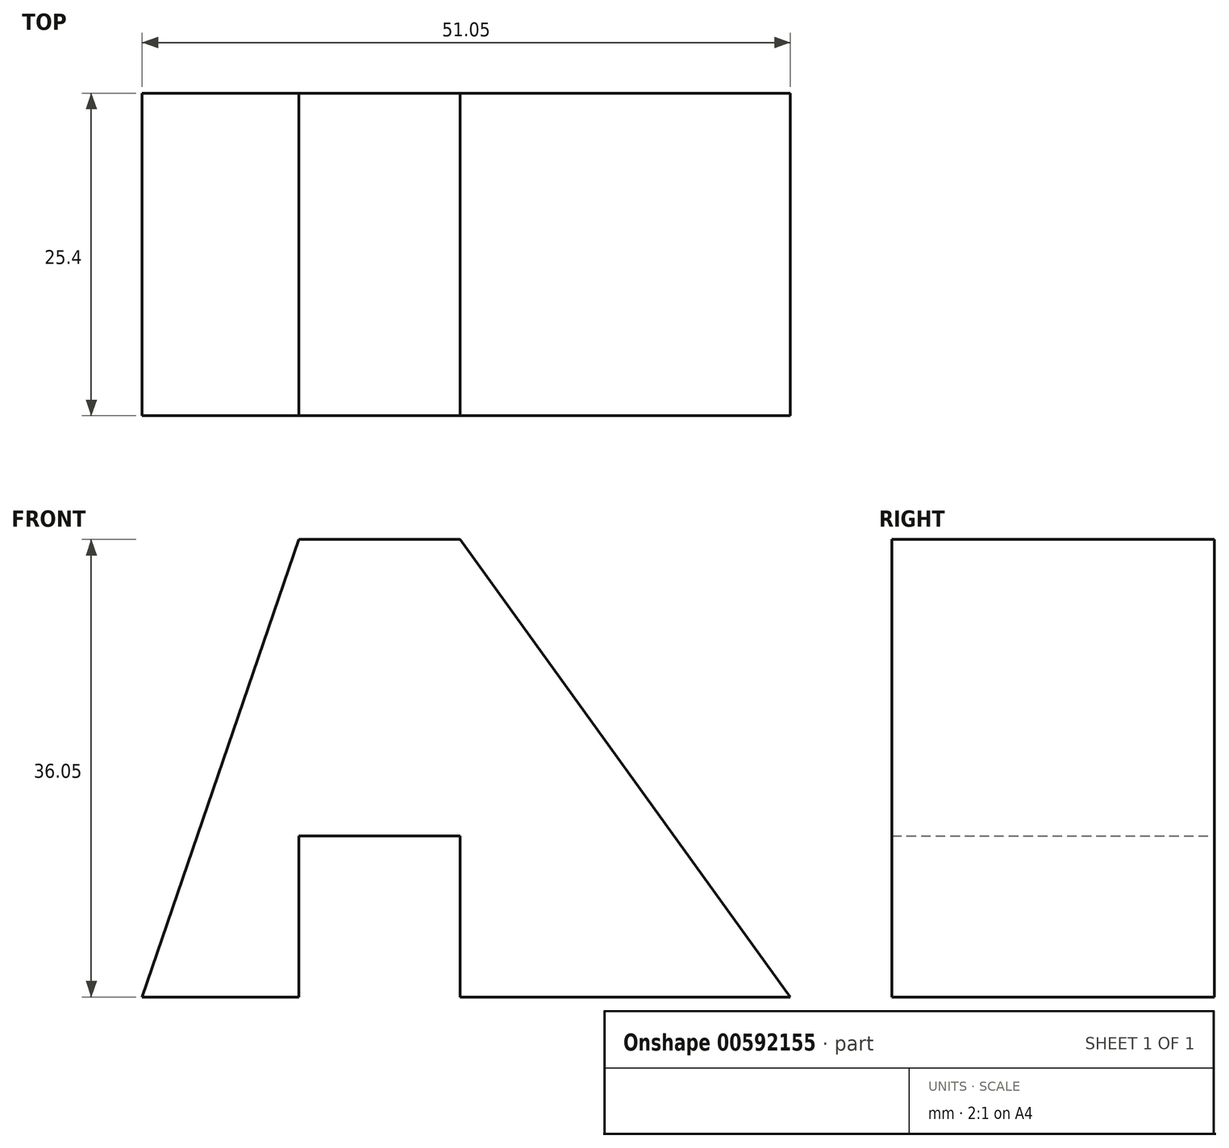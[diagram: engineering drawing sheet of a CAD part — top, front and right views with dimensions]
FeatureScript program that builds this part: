
annotation { "Feature Type Name" : "Feature", "Feature Type Description" : "" }
export const myFeature = defineFeature(function(context is Context, id is Id, definition is map)
    precondition{}
    {
        {
            var Q0;
            Q0=qCreatedBy(makeId("Front.planeOp"),FACE);
            var sketch = newSketch(context, id + "F0", { "sketchPlane" : qUnion([Q0])});
            skLineSegment(sketch, "E0", {"start": v(0, 0) * mm, "end": v(26.01, 0) * mm});
            skLineSegment(sketch, "E1", {"start": v(26.01, 0) * mm, "end": v(0, 36.05) * mm});
            skLineSegment(sketch, "E2", {"start": v(0, 36.05) * mm, "end": v(-12.7, 36.05) * mm});
            skLineSegment(sketch, "E3", {"start": v(-12.7, 36.05) * mm, "end": v(-25.04, 0) * mm});
            skLineSegment(sketch, "E4", {"start": v(-25.04, 0) * mm, "end": v(-12.7, 0) * mm});
            skLineSegment(sketch, "E5", {"start": v(-12.7, 0) * mm, "end": v(-12.7, 12.7) * mm});
            skLineSegment(sketch, "E6", {"start": v(-12.7, 12.7) * mm, "end": v(0, 12.7) * mm});
            skLineSegment(sketch, "E7", {"start": v(0, 12.7) * mm, "end": v(0, 0) * mm});
            skSolve(sketch);
        }
        {
            var Q0;
            Q0 = qSketchRegion(id + "F0", true);
            extrude(context, id + "F1", {"entities" : qUnion([Q0]), "depth" : 25.4 * mm, "offsetDistance" : 25.4 * mm});
        }
    });
